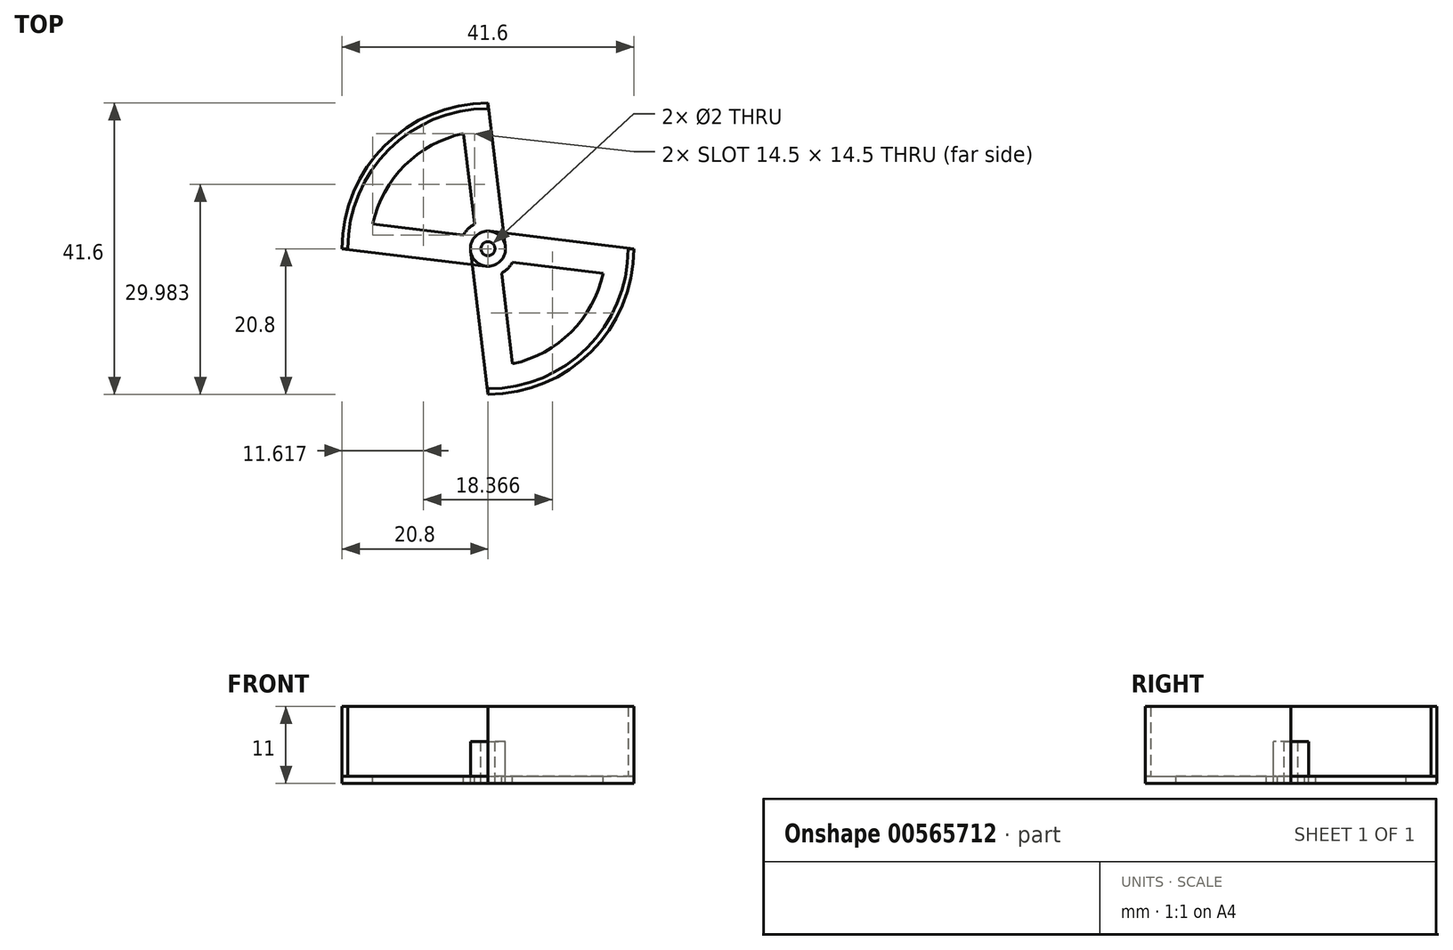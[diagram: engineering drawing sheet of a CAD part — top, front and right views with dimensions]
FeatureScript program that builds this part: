
annotation { "Feature Type Name" : "Feature", "Feature Type Description" : "" }
export const myFeature = defineFeature(function(context is Context, id is Id, definition is map)
    precondition{}
    {
        {
            var Q0;
            Q0=qCreatedBy(makeId("Top.planeOp"),FACE);
            var sketch = newSketch(context, id + "F0", { "sketchPlane" : qUnion([Q0])});
            skArc(sketch, "E0", {"start": v(0, 20) * mm, "mid": v(-14.14, 14.14) * mm, "end": v(-20, 0) * mm});
            skLineSegment(sketch, "E1", {"start": v(-20, 0) * mm, "end": v(0, 0) * mm});
            skLineSegment(sketch, "E2", {"start": v(0, 0) * mm, "end": v(0, 20) * mm});
            skArc(sketch, "E3", {"start": v(0, 20.8) * mm, "mid": v(-14.7, 14.7) * mm, "end": v(-20.8, 0) * mm});
            skLineSegment(sketch, "E4", {"start": v(-20, 0) * mm, "end": v(-20.8, 0) * mm});
            skLineSegment(sketch, "E5", {"start": v(0, 20) * mm, "end": v(0, 20.8) * mm});
            skSolve(sketch);
        }
        {
            var Q0;
            Q0=makeQuery(id+"F0.imprint","IMPRINT",FACE,{"disambiguationData":[TD([[makeQuery(id+"F0.imprint","IMPRINT",EDGE,{"derivedFrom":sQuery(id+"F0.wireOp",EDGE,"E0")}),-1.0]])]});
            extrude(context, id + "F1", {"entities" : qUnion([Q0]), "depth" : 10 * mm, "offsetDistance" : 25 * mm});
        }
        {
            var Q0;
            Q0=qCreatedBy(makeId("Top.planeOp"),FACE);
            var sketch = newSketch(context, id + "F2", { "sketchPlane" : qUnion([Q0])});
            skArc(sketch, "E6", {"start": v(0, 20.8) * mm, "mid": v(-14.7, 14.7) * mm, "end": v(-20.8, 0) * mm});
            skArc(sketch, "E7", {"start": v(-3.5, 16.43) * mm, "mid": v(-11.88, 11.88) * mm, "end": v(-16.43, 3.5) * mm});
            skLineSegment(sketch, "E8", {"start": v(-16.43, 3.5) * mm, "end": v(-3.5, 1.93) * mm});
            skArc(sketch, "E9", {"start": v(-0.3, -2.48) * mm, "mid": v(1.77, -1.77) * mm, "end": v(2.48, 0.3) * mm});
            skCircle(sketch, "E10", {"center": v(0, 0) * mm, "radius": 1 * mm});
            skLineSegment(sketch, "E11", {"start": v(-20.8, 0) * mm, "end": v(-0.3, -2.48) * mm});
            skLineSegment(sketch, "E12", {"start": v(0, 20.8) * mm, "end": v(2.48, 0.3) * mm});
            skArc(sketch, "E13", {"start": v(-1.93, 3.5) * mm, "mid": v(-2.83, 2.83) * mm, "end": v(-3.5, 1.93) * mm});
            skLineSegment(sketch, "E14.trimOffspring", {"start": v(-1.93, 3.5) * mm, "end": v(-3.5, 16.43) * mm});
            skSolve(sketch);
        }
        {
            var Q0;
            Q0 = qSketchRegion(id + "F2", true);
            extrude(context, id + "F3", {"entities" : qUnion([Q0]), "operationType" : NewBodyOperationType.ADD, "oppositeDirection" : true, "depth" : 1 * mm, "offsetDistance" : 25 * mm});
        }
        {
            var Q0;
            Q0=makeQuery(id+"F3.opExtrude","CAP_FACE",FACE,{"disambiguationData":[OSD([sQuery(id+"F2.wireOp",EDGE,"E6"),sQuery(id+"F2.wireOp",EDGE,"E7"),sQuery(id+"F2.wireOp",EDGE,"E8"),sQuery(id+"F2.wireOp",EDGE,"E9"),sQuery(id+"F2.wireOp",EDGE,"E10"),sQuery(id+"F2.wireOp",EDGE,"E11"),sQuery(id+"F2.wireOp",EDGE,"E12"),sQuery(id+"F2.wireOp",EDGE,"E13"),sQuery(id+"F2.wireOp",EDGE,"E14.trimOffspring")])],"isStart":true});
            var sketch = newSketch(context, id + "F4", { "sketchPlane" : qUnion([Q0])});
            skCircle(sketch, "E15", {"center": v(0, 0) * mm, "radius": 2.5 * mm});
            skCircle(sketch, "E16", {"center": v(0, 0) * mm, "radius": 1 * mm});
            skSolve(sketch);
        }
        {
            var Q0;
            Q0 = qSketchRegion(id + "F4", true);
            extrude(context, id + "F5", {"entities" : qUnion([Q0]), "operationType" : NewBodyOperationType.ADD, "depth" : 5 * mm, "offsetDistance" : 25 * mm});
        }
        {
            var Q0;
            Q0=makeQuery(id+"F1.opExtrude","SWEPT_BODY",BODY,{"disambiguationData":[OSD([sQuery(id+"F0.wireOp",EDGE,"E0"),sQuery(id+"F0.wireOp",EDGE,"E3"),sQuery(id+"F0.wireOp",EDGE,"E4"),sQuery(id+"F0.wireOp",EDGE,"E5")])]});
            var Q1;
            Q1=makeQuery(id+"F5.opExtrude","CAP_EDGE",EDGE,{"disambiguationData":[OSD([sQuery(id+"F4.wireOp",EDGE,"E16")])],"isStart":false});
            circularPattern(context, id + "F6", {"entities" : qUnion([Q0]), "axis" : qUnion([Q1]), "angle" : 360 * degree, "instanceCount" : 2, "equalSpace" : true});
        }
    });
